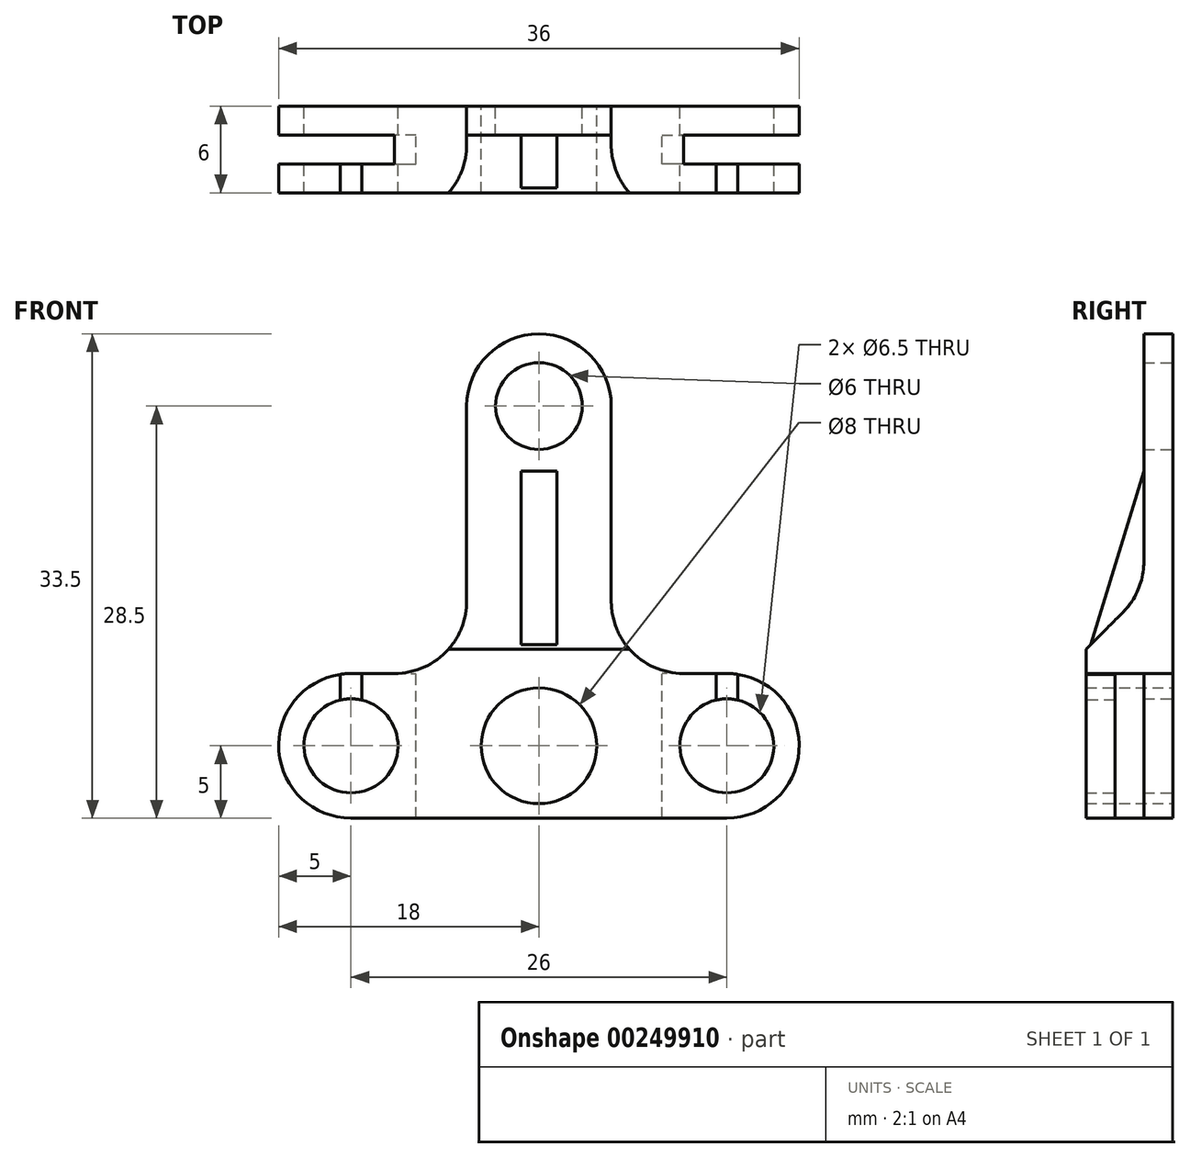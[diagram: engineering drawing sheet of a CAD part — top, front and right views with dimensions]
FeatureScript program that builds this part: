
annotation { "Feature Type Name" : "Feature", "Feature Type Description" : "" }
export const myFeature = defineFeature(function(context is Context, id is Id, definition is map)
    precondition{}
    {
        {
            var Q0;
            Q0=qCreatedBy(makeId("Front.planeOp"),FACE);
            var sketch = newSketch(context, id + "F0", { "sketchPlane" : qUnion([Q0])});
            skCircle(sketch, "E0", {"center": v(0, 0) * mm, "radius": 4 * mm});
            skCircle(sketch, "E1", {"center": v(13, 0) * mm, "radius": 3.25 * mm});
            skCircle(sketch, "E2", {"center": v(-13, 0) * mm, "radius": 3.25 * mm});
            skArc(sketch, "E3", {"start": v(-13, 5) * mm, "mid": v(-18, 0) * mm, "end": v(-13, -5) * mm});
            skCircle(sketch, "E4", {"center": v(13, 0) * mm, "radius": 5 * mm});
            skCircle(sketch, "E5", {"center": v(0, 23.5) * mm, "radius": 3 * mm});
            skArc(sketch, "E6", {"start": v(5, 23.5) * mm, "mid": v(0, 28.5) * mm, "end": v(-5, 23.5) * mm});
            skLineSegment(sketch, "E7", {"start": v(-5, 23.5) * mm, "end": v(-5, 10) * mm});
            skLineSegment(sketch, "E8", {"start": v(-13, 5) * mm, "end": v(-10, 5) * mm});
            skLineSegment(sketch, "E9", {"start": v(-13, -5) * mm, "end": v(13, -5) * mm});
            skArc(sketch, "E10", {"start": v(-10, 5) * mm, "mid": v(-6.46, 6.46) * mm, "end": v(-5, 10) * mm});
            skLineSegment(sketch, "E11.MirrorCS", {"start": v(5, 23.5) * mm, "end": v(5, 10) * mm});
            skArc(sketch, "E12.MirrorCS", {"start": v(10, 5) * mm, "mid": v(6.46, 6.46) * mm, "end": v(5, 10) * mm});
            skLineSegment(sketch, "E13.MirrorCS", {"start": v(13, 5) * mm, "end": v(10, 5) * mm});
            skSolve(sketch);
        }
        {
            var Q0;
            Q0=makeQuery(id+"F0.imprint","IMPRINT",FACE,{"disambiguationData":[TD([[makeQuery(id+"F0.imprint","IMPRINT",EDGE,{"derivedFrom":sQuery(id+"F0.wireOp",EDGE,"E0")}),-1.0]])]});
            var Q1;
            Q1=makeQuery(id+"F0.imprint","IMPRINT",FACE,{"disambiguationData":[TD([[makeQuery(id+"F0.imprint","IMPRINT",EDGE,{"derivedFrom":sQuery(id+"F0.wireOp",EDGE,"E1")}),-1.0]])]});
            extrude(context, id + "F1", {"entities" : qUnion([Q0, Q1]), "endBound" : BoundingType.SYMMETRIC, "depth" : 6 * mm});
        }
        {
            var Q0;
            Q0=makeQuery(id+"F1.opExtrude","SWEPT_FACE",FACE,{"disambiguationData":[OSD([sQuery(id+"F0.wireOp",EDGE,"E13.MirrorCS")])]});
            var sketch = newSketch(context, id + "F2", { "sketchPlane" : qUnion([Q0])});
            skLineSegment(sketch, "E14", {"start": v(18, 3) * mm, "end": v(18, -3) * mm});
            skLineSegment(sketch, "E15", {"start": v(18, -1) * mm, "end": v(8.5, -1) * mm});
            skLineSegment(sketch, "E16", {"start": v(8.5, 1) * mm, "end": v(18, 1) * mm});
            skLineSegment(sketch, "E17", {"start": v(18, -1) * mm, "end": v(18, 1) * mm});
            skLineSegment(sketch, "E18", {"start": v(8.5, -1) * mm, "end": v(8.5, 1) * mm});
            skLineSegment(sketch, "E19.MirrorCS", {"start": v(-8.5, 1) * mm, "end": v(-18, 1) * mm});
            skLineSegment(sketch, "E20.MirrorCS", {"start": v(-18, -1) * mm, "end": v(-8.5, -1) * mm});
            skLineSegment(sketch, "E21.MirrorCS", {"start": v(-8.5, -1) * mm, "end": v(-8.5, 1) * mm});
            skLineSegment(sketch, "E22.MirrorCS", {"start": v(-18, -1) * mm, "end": v(-18, 1) * mm});
            skSolve(sketch);
        }
        {
            var Q0;
            Q0 = qSketchRegion(id + "F2", true);
            extrude(context, id + "F3", {"entities" : qUnion([Q0]), "operationType" : NewBodyOperationType.REMOVE, "endBound" : BoundingType.THROUGH_ALL, "oppositeDirection" : true, "depth" : 25 * mm});
        }
        {
            var Q0;
            Q0=makeQuery(id+"F1.opExtrude","CAP_FACE",FACE,{"disambiguationData":[OSD([sQuery(id+"F0.wireOp",EDGE,"E0"),sQuery(id+"F0.wireOp",EDGE,"E1"),sQuery(id+"F0.wireOp",EDGE,"E2"),sQuery(id+"F0.wireOp",EDGE,"E3"),sQuery(id+"F0.wireOp",EDGE,"E4"),sQuery(id+"F0.wireOp",EDGE,"E5"),sQuery(id+"F0.wireOp",EDGE,"E6"),sQuery(id+"F0.wireOp",EDGE,"E7"),sQuery(id+"F0.wireOp",EDGE,"E8"),sQuery(id+"F0.wireOp",EDGE,"E9"),sQuery(id+"F0.wireOp",EDGE,"E10"),sQuery(id+"F0.wireOp",EDGE,"E11.MirrorCS"),sQuery(id+"F0.wireOp",EDGE,"E12.MirrorCS"),sQuery(id+"F0.wireOp",EDGE,"E13.MirrorCS")])],"isStart":false});
            var sketch = newSketch(context, id + "F4", { "sketchPlane" : qUnion([Q0])});
            skArc(sketch, "E23.0", {"start": v(-13.75, -3.16) * mm, "mid": v(-13, -3.25) * mm, "end": v(-12.25, -3.16) * mm});
            skLineSegment(sketch, "E24", {"start": v(-13.75, -4.94) * mm, "end": v(-13.75, -3.16) * mm});
            skLineSegment(sketch, "E25", {"start": v(-13, -7.2) * mm, "end": v(-13, 7.48) * mm, "construction": true});
            skLineSegment(sketch, "E26", {"start": v(-12.25, -5) * mm, "end": v(-12.25, -3.16) * mm});
            skArc(sketch, "E27.0", {"start": v(-13, 5) * mm, "mid": v(-13.38, 4.99) * mm, "end": v(-13.75, 4.94) * mm});
            skLineSegment(sketch, "E28.0", {"start": v(-13, 5) * mm, "end": v(-12.25, 5) * mm});
            skLineSegment(sketch, "E29.0", {"start": v(-13, -5) * mm, "end": v(-12.25, -5) * mm});
            skLineSegment(sketch, "E30.trimOffspring", {"start": v(-13.75, 3.16) * mm, "end": v(-13.75, 4.94) * mm});
            skLineSegment(sketch, "E31.trimOffspring", {"start": v(-12.25, 3.16) * mm, "end": v(-12.25, 5) * mm});
            skPoint(sketch, "E32.orphan", {"position": v(-10, 5) * mm});
            skArc(sketch, "E33.trimOffspring", {"start": v(-13.75, -4.94) * mm, "mid": v(-13.38, -4.99) * mm, "end": v(-13, -5) * mm});
            skArc(sketch, "E34.trimOffspring", {"start": v(-12.25, 3.16) * mm, "mid": v(-13, 3.25) * mm, "end": v(-13.75, 3.16) * mm});
            skPoint(sketch, "E35.orphan", {"position": v(13, -5) * mm});
            skLineSegment(sketch, "E36.MirrorCS", {"start": v(13.75, 3.16) * mm, "end": v(13.75, 4.94) * mm});
            skLineSegment(sketch, "E37.MirrorCS", {"start": v(12.25, 3.16) * mm, "end": v(12.25, 5) * mm});
            skArc(sketch, "E38.MirrorCS", {"start": v(13, 5) * mm, "mid": v(13.38, 4.99) * mm, "end": v(13.75, 4.94) * mm});
            skLineSegment(sketch, "E39.MirrorCS", {"start": v(13, 5) * mm, "end": v(12.25, 5) * mm});
            skArc(sketch, "E40.MirrorCS", {"start": v(12.25, 3.16) * mm, "mid": v(13, 3.25) * mm, "end": v(13.75, 3.16) * mm});
            skArc(sketch, "E41.MirrorCS", {"start": v(13.75, -3.16) * mm, "mid": v(13, -3.25) * mm, "end": v(12.25, -3.16) * mm});
            skLineSegment(sketch, "E42.MirrorCS", {"start": v(13.75, -4.94) * mm, "end": v(13.75, -3.16) * mm});
            skArc(sketch, "E43.MirrorCS", {"start": v(13.75, -4.94) * mm, "mid": v(13.38, -4.99) * mm, "end": v(13, -5) * mm});
            skLineSegment(sketch, "E44.MirrorCS", {"start": v(13, -5) * mm, "end": v(12.25, -5) * mm});
            skLineSegment(sketch, "E45.MirrorCS", {"start": v(12.25, -5) * mm, "end": v(12.25, -3.16) * mm});
            skSolve(sketch);
        }
        {
            var Q0;
            Q0=makeQuery(id+"F4.imprint","IMPRINT",FACE,{"disambiguationData":[TD([[makeQuery(id+"F4.imprint","IMPRINT",EDGE,{"derivedFrom":sQuery(id+"F4.wireOp",EDGE,"E27.0")}),1.0]])]});
            var Q1;
            Q1=makeQuery(id+"F4.imprint","IMPRINT",FACE,{"disambiguationData":[TD([[makeQuery(id+"F4.imprint","IMPRINT",EDGE,{"derivedFrom":sQuery(id+"F4.wireOp",EDGE,"E36.MirrorCS")}),1.0]])]});
            extrude(context, id + "F5", {"entities" : qUnion([Q0, Q1]), "operationType" : NewBodyOperationType.REMOVE, "oppositeDirection" : true, "depth" : 2 * mm});
        }
        {
            var Q0;
            Q0=makeQuery(id+"F1.opExtrude","SWEPT_FACE",FACE,{"disambiguationData":[OSD([sQuery(id+"F0.wireOp",EDGE,"E11.MirrorCS")])]});
            var sketch = newSketch(context, id + "F6", { "sketchPlane" : qUnion([Q0])});
            skLineSegment(sketch, "E46", {"start": v(-3, 28.5) * mm, "end": v(3, 28.5) * mm});
            skLineSegment(sketch, "E47.0", {"start": v(-3, 23.5) * mm, "end": v(-3, 10) * mm});
            skLineSegment(sketch, "E48.0", {"start": v(3, 23.5) * mm, "end": v(3, 10) * mm});
            skLineSegment(sketch, "E49.0", {"start": v(3, 23.5) * mm, "end": v(3, 28.5) * mm});
            skLineSegment(sketch, "E50.0", {"start": v(-3, 23.5) * mm, "end": v(-3, 28.5) * mm});
            skLineSegment(sketch, "E51.0", {"start": v(-3, 5) * mm, "end": v(-3, 10) * mm});
            skLineSegment(sketch, "E52.0", {"start": v(-1, 4.94) * mm, "end": v(-3, 4.94) * mm});
            skLineSegment(sketch, "E53.0", {"start": v(-1, 5) * mm, "end": v(1, 5) * mm});
            skLineSegment(sketch, "E54.0", {"start": v(1, 5) * mm, "end": v(3, 5) * mm});
            skLineSegment(sketch, "E55.0", {"start": v(3, 5) * mm, "end": v(3, 10) * mm});
            skLineSegment(sketch, "E56", {"start": v(-3, 5) * mm, "end": v(-3, 6.68) * mm});
            skLineSegment(sketch, "E57", {"start": v(1, 5) * mm, "end": v(1, 28.5) * mm});
            skLineSegment(sketch, "E58", {"start": v(-3, 6.68) * mm, "end": v(-0.46, 9.21) * mm});
            skArc(sketch, "E59", {"start": v(-0.46, 9.21) * mm, "mid": v(0.62, 10.83) * mm, "end": v(1, 12.75) * mm});
            skSolve(sketch);
        }
        {
            var Q0;
            {var subQ0=sQuery(id+"F6.wireOp",EDGE,"E51.0");Q0=makeQuery(id+"F6.imprint","IMPRINT",FACE,{"disambiguationData":[TD([[makeQuery(id+"F6.imprint","IMPRINT",EDGE,{"derivedFrom":subQ0}),-1.0]])]});}
            var Q1;
            {var subQ0=sQuery(id+"F6.wireOp",EDGE,"E47.0");Q1=makeQuery(id+"F6.imprint","IMPRINT",FACE,{"disambiguationData":[TD([[makeQuery(id+"F6.imprint","IMPRINT",EDGE,{"derivedFrom":subQ0}),1.0]])]});}
            var Q2;
            {var subQ0=sQuery(id+"F6.wireOp",EDGE,"E50.0");Q2=makeQuery(id+"F6.imprint","IMPRINT",FACE,{"disambiguationData":[TD([[makeQuery(id+"F6.imprint","IMPRINT",EDGE,{"derivedFrom":subQ0}),-1.0]])]});}
            extrude(context, id + "F7", {"entities" : qUnion([Q0, Q1, Q2]), "operationType" : NewBodyOperationType.REMOVE, "oppositeDirection" : true, "depth" : 25 * mm});
        }
        {
            var Q0;
            Q0=makeQuery(id+"F7.boolean.opBoolean","COPY",FACE,{"derivedFrom":makeQuery(id+"F7.opExtrude","CAP_FACE",FACE,{"disambiguationData":[OSD([sQuery(id+"F6.wireOp",EDGE,"E46"),sQuery(id+"F6.wireOp",EDGE,"E47.0"),sQuery(id+"F6.wireOp",EDGE,"E50.0"),sQuery(id+"F6.wireOp",EDGE,"E51.0"),sQuery(id+"F6.wireOp",EDGE,"E57"),sQuery(id+"F6.wireOp",EDGE,"E58"),sQuery(id+"F6.wireOp",EDGE,"E59")])],"isStart":true})});
            extrude(context, id + "F8", {"entities" : qUnion([Q0]), "operationType" : NewBodyOperationType.REMOVE, "oppositeDirection" : true, "depth" : 25 * mm});
        }
        {
            var Q0;
            Q0=makeQuery(id+"F1.opExtrude","SWEPT_FACE",FACE,{"disambiguationData":[OSD([sQuery(id+"F0.wireOp",EDGE,"E11.MirrorCS")])]});
            cPlane(context, id + "F9", {"entities" : qUnion([Q0]), "cplaneType" : CPlaneType.OFFSET, "offset" : 5 * mm, "oppositeDirection" : true, "width" : 150 * mm, "height" : 150 * mm});
        }
        {
            var Q0;
            Q0=qCreatedBy(id+"F9.planeOp",FACE);
            var sketch = newSketch(context, id + "F10", { "sketchPlane" : qUnion([Q0])});
            skPoint(sketch, "E60.0", {"position": v(-3, 6.68) * mm});
            skPoint(sketch, "E61.orphan", {"position": v(1, 23.5) * mm});
            skPoint(sketch, "E62.0.start.orphan", {"position": v(1, 12.75) * mm});
            skLineSegment(sketch, "E63.0", {"start": v(1, 12.75) * mm, "end": v(1, 23.5) * mm});
            skArc(sketch, "E64.0", {"start": v(0.18, 10) * mm, "mid": v(0.79, 11.31) * mm, "end": v(1, 12.75) * mm});
            skLineSegment(sketch, "E65.0", {"start": v(-3, 6.68) * mm, "end": v(-0.46, 9.21) * mm});
            skArc(sketch, "E66.0", {"start": v(0.18, 10) * mm, "mid": v(-0.12, 9.6) * mm, "end": v(-0.46, 9.21) * mm});
            skPoint(sketch, "E67", {"position": v(1, 19) * mm});
            skLineSegment(sketch, "E68", {"start": v(1, 19) * mm, "end": v(-2.67, 7.01) * mm});
            skSolve(sketch);
        }
        {
            var Q0;
            {var subQ3=sQuery(id+"F10.wireOp",EDGE,"E64.0");Q0=makeQuery(id+"F10.imprint","IMPRINT",FACE,{"disambiguationData":[TD([[makeQuery(id+"F10.imprint","IMPRINT",EDGE,{"derivedFrom":subQ3}),1.0]])]});}
            extrude(context, id + "F11", {"entities" : qUnion([Q0]), "operationType" : NewBodyOperationType.ADD, "endBound" : BoundingType.SYMMETRIC, "depth" : 2.5 * mm});
        }
    });
